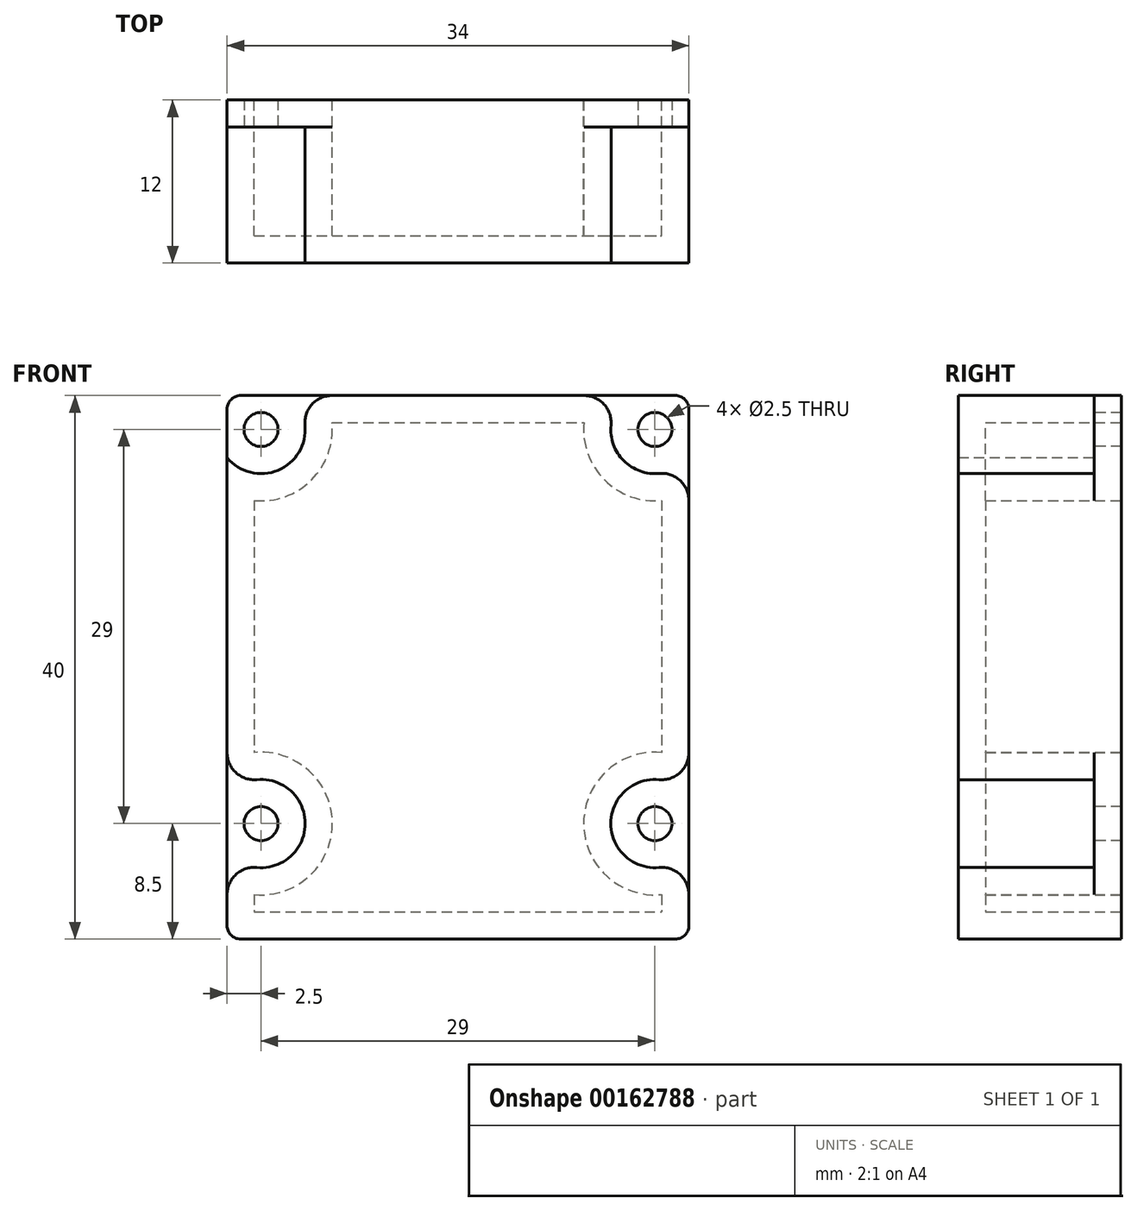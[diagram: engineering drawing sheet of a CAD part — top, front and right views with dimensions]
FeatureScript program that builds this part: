
annotation { "Feature Type Name" : "Feature", "Feature Type Description" : "" }
export const myFeature = defineFeature(function(context is Context, id is Id, definition is map)
    precondition{}
    {
        {
            var Q0;
            Q0=qCreatedBy(makeId("Front.planeOp"),FACE);
            var sketch = newSketch(context, id + "F0", { "sketchPlane" : qUnion([Q0])});
            skLineSegment(sketch, "E0.bottom", {"start": v(-16, 20) * mm, "end": v(16, 20) * mm});
            skLineSegment(sketch, "E0.top", {"start": v(-16, -20) * mm, "end": v(16, -20) * mm});
            skLineSegment(sketch, "E0.left", {"start": v(-17, 19) * mm, "end": v(-17, -19) * mm});
            skLineSegment(sketch, "E0.right", {"start": v(17, 19) * mm, "end": v(17, -19) * mm});
            skPoint(sketch, "E1.visualSharp", {"position": v(-17, 20) * mm});
            skArc(sketch, "E1.filletArc", {"start": v(-16, 20) * mm, "mid": v(-16.7, 19.7) * mm, "end": v(-17, 19) * mm});
            skPoint(sketch, "E2.visualSharp", {"position": v(17, 20) * mm});
            skArc(sketch, "E2.filletArc", {"start": v(17, 19) * mm, "mid": v(16.7, 19.7) * mm, "end": v(16, 20) * mm});
            skPoint(sketch, "E3.visualSharp", {"position": v(17, -20) * mm});
            skArc(sketch, "E3.filletArc", {"start": v(16, -20) * mm, "mid": v(16.7, -19.7) * mm, "end": v(17, -19) * mm});
            skPoint(sketch, "E4.visualSharp", {"position": v(-17, -20) * mm});
            skArc(sketch, "E4.filletArc", {"start": v(-17, -19) * mm, "mid": v(-16.7, -19.7) * mm, "end": v(-16, -20) * mm});
            skSolve(sketch);
        }
        {
            var Q0;
            Q0 = qSketchRegion(id + "F0", true);
            extrude(context, id + "F1", {"entities" : qUnion([Q0]), "depth" : 12 * mm, "offsetDistance" : 25 * mm});
        }
        {
            var Q0;
            Q0=makeQuery(id+"F1.opExtrude","CAP_FACE",FACE,{"disambiguationData":[OSD([sQuery(id+"F0.wireOp",EDGE,"E0.bottom"),sQuery(id+"F0.wireOp",EDGE,"E0.top"),sQuery(id+"F0.wireOp",EDGE,"E0.left"),sQuery(id+"F0.wireOp",EDGE,"E0.right"),sQuery(id+"F0.wireOp",EDGE,"E1.filletArc"),sQuery(id+"F0.wireOp",EDGE,"E2.filletArc"),sQuery(id+"F0.wireOp",EDGE,"E3.filletArc"),sQuery(id+"F0.wireOp",EDGE,"E4.filletArc")])],"isStart":true});
            cPlane(context, id + "F2", {"entities" : qUnion([Q0]), "cplaneType" : CPlaneType.OFFSET, "offset" : 2 * mm, "oppositeDirection" : true, "width" : 150 * mm, "height" : 150 * mm});
        }
        {
            var Q0;
            Q0=qCreatedBy(id+"F2.planeOp",FACE);
            var sketch = newSketch(context, id + "F3", { "sketchPlane" : qUnion([Q0])});
            skPoint(sketch, "E5", {"position": v(14.5, 17.5) * mm});
            skPoint(sketch, "E6", {"position": v(-14.5, 17.5) * mm});
            skPoint(sketch, "E7", {"position": v(-14.5, -11.5) * mm});
            skPoint(sketch, "E8", {"position": v(14.5, -11.5) * mm});
            skCircle(sketch, "E9", {"center": v(-14.5, 17.5) * mm, "radius": 3.25 * mm});
            skCircle(sketch, "E10", {"center": v(14.5, 17.5) * mm, "radius": 3.25 * mm});
            skCircle(sketch, "E11", {"center": v(-14.5, -11.5) * mm, "radius": 3.25 * mm});
            skCircle(sketch, "E12", {"center": v(14.5, -11.5) * mm, "radius": 3.25 * mm});
            skSolve(sketch);
        }
        {
            var Q0;
            Q0 = qSketchRegion(id + "F3", true);
            extrude(context, id + "F4", {"entities" : qUnion([Q0]), "operationType" : NewBodyOperationType.REMOVE, "oppositeDirection" : true, "depth" : 25 * mm, "offsetDistance" : 25 * mm});
        }
        {
            var Q0;
            Q0=sQuery(id+"F3.wireOp",VERTEX,"E5");
            var Q1;
            Q1=sQuery(id+"F3.wireOp",VERTEX,"E6");
            var Q2;
            Q2=sQuery(id+"F3.wireOp",VERTEX,"E8");
            var Q3;
            Q3=sQuery(id+"F3.wireOp",VERTEX,"E7");
            var Q4;
            Q4=makeQuery(id+"F1.opExtrude","SWEPT_BODY",BODY,{"disambiguationData":[OSD([sQuery(id+"F0.wireOp",EDGE,"E0.bottom"),sQuery(id+"F0.wireOp",EDGE,"E0.top"),sQuery(id+"F0.wireOp",EDGE,"E0.left"),sQuery(id+"F0.wireOp",EDGE,"E0.right"),sQuery(id+"F0.wireOp",EDGE,"E1.filletArc"),sQuery(id+"F0.wireOp",EDGE,"E2.filletArc"),sQuery(id+"F0.wireOp",EDGE,"E3.filletArc"),sQuery(id+"F0.wireOp",EDGE,"E4.filletArc")])]});
            hole(context, id + "F5", {"style" : HoleStyle.SIMPLE, "endStyle" : HoleEndStyle.THROUGH, "oppositeDirection" : true, "standardTappedOrClearance" : lookupTablePath({ "standard" : "ISO", "engagement" : "75%", "pitch" : "0.5 mm", "size" : "M3", "type" : "Tapped" }), "standardBlindInLast" : lookupTablePath({ "standard" : "ISO", "engagement" : "75%", "pitch" : "0.5 mm", "size" : "M3", "type" : "Tapped" }), "holeDiameter" : 2.5 * mm, "showTappedDepth" : true, "isTappedThrough" : true, "tappedDepth" : 12 * mm, "tapClearance" : 3, "locations" : qUnion([Q0, Q1, Q2, Q3]), "scope" : qUnion([Q4]), "majorDiameter" : 3 * mm});
        }
        {
            var Q0;
            Q0=makeQuery(id+"F1.opExtrude","CAP_FACE",FACE,{"disambiguationData":[OSD([sQuery(id+"F0.wireOp",EDGE,"E0.bottom"),sQuery(id+"F0.wireOp",EDGE,"E0.top"),sQuery(id+"F0.wireOp",EDGE,"E0.left"),sQuery(id+"F0.wireOp",EDGE,"E0.right"),sQuery(id+"F0.wireOp",EDGE,"E1.filletArc"),sQuery(id+"F0.wireOp",EDGE,"E2.filletArc"),sQuery(id+"F0.wireOp",EDGE,"E3.filletArc"),sQuery(id+"F0.wireOp",EDGE,"E4.filletArc")])],"isStart":true});
            shell(context, id + "F6", {"entities" : qUnion([Q0]), "thickness" : 2 * mm});
        }
        {
            var Q0;
            Q0=makeQuery(id+"F4.boolean.opBoolean","INTERSECT",EDGE,{"derivedFrom":[makeQuery(id+"F1.opExtrude","SWEPT_FACE",FACE,{"disambiguationData":[OSD([sQuery(id+"F0.wireOp",EDGE,"E0.right")])]}),makeQuery(id+"F4.opExtrude","SWEPT_FACE",FACE,{"disambiguationData":[OSD([sQuery(id+"F3.wireOp",EDGE,"E9")])]})]});
            var Q1;
            Q1=makeQuery(id+"F4.boolean.opBoolean","INTERSECT",EDGE,{"derivedFrom":[makeQuery(id+"F1.opExtrude","SWEPT_FACE",FACE,{"disambiguationData":[OSD([sQuery(id+"F0.wireOp",EDGE,"E0.bottom")])]}),makeQuery(id+"F4.opExtrude","SWEPT_FACE",FACE,{"disambiguationData":[OSD([sQuery(id+"F3.wireOp",EDGE,"E9")])]})]});
            var Q2;
            Q2=makeQuery(id+"F4.boolean.opBoolean","INTERSECT",EDGE,{"derivedFrom":[makeQuery(id+"F1.opExtrude","SWEPT_FACE",FACE,{"disambiguationData":[OSD([sQuery(id+"F0.wireOp",EDGE,"E0.bottom")])]}),makeQuery(id+"F4.opExtrude","SWEPT_FACE",FACE,{"disambiguationData":[OSD([sQuery(id+"F3.wireOp",EDGE,"E10")])]})]});
            var Q3;
            Q3=makeQuery(id+"F4.boolean.opBoolean","INTERSECT",EDGE,{"disambiguationData":[OD(1.0)],"derivedFrom":[makeQuery(id+"F1.opExtrude","SWEPT_FACE",FACE,{"disambiguationData":[OSD([sQuery(id+"F0.wireOp",EDGE,"E0.right")])]}),makeQuery(id+"F4.opExtrude","SWEPT_FACE",FACE,{"disambiguationData":[OSD([sQuery(id+"F3.wireOp",EDGE,"E11")])]})]});
            var Q4;
            Q4=makeQuery(id+"F4.boolean.opBoolean","INTERSECT",EDGE,{"disambiguationData":[OD(0.0)],"derivedFrom":[makeQuery(id+"F1.opExtrude","SWEPT_FACE",FACE,{"disambiguationData":[OSD([sQuery(id+"F0.wireOp",EDGE,"E0.right")])]}),makeQuery(id+"F4.opExtrude","SWEPT_FACE",FACE,{"disambiguationData":[OSD([sQuery(id+"F3.wireOp",EDGE,"E11")])]})]});
            var Q5;
            Q5=makeQuery(id+"F4.boolean.opBoolean","INTERSECT",EDGE,{"disambiguationData":[OD(1.0)],"derivedFrom":[makeQuery(id+"F1.opExtrude","SWEPT_FACE",FACE,{"disambiguationData":[OSD([sQuery(id+"F0.wireOp",EDGE,"E0.left")])]}),makeQuery(id+"F4.opExtrude","SWEPT_FACE",FACE,{"disambiguationData":[OSD([sQuery(id+"F3.wireOp",EDGE,"E12")])]})]});
            var Q6;
            Q6=makeQuery(id+"F4.boolean.opBoolean","INTERSECT",EDGE,{"disambiguationData":[OD(0.0)],"derivedFrom":[makeQuery(id+"F1.opExtrude","SWEPT_FACE",FACE,{"disambiguationData":[OSD([sQuery(id+"F0.wireOp",EDGE,"E0.left")])]}),makeQuery(id+"F4.opExtrude","SWEPT_FACE",FACE,{"disambiguationData":[OSD([sQuery(id+"F3.wireOp",EDGE,"E12")])]})]});
            fillet(context, id + "F7", {"entities" : qUnion([Q0, Q1, Q2, Q3, Q4, Q5, Q6]), "radius" : 2 * mm, "tangentPropagation" : true, "allowEdgeOverflow" : false});
        }
    });
